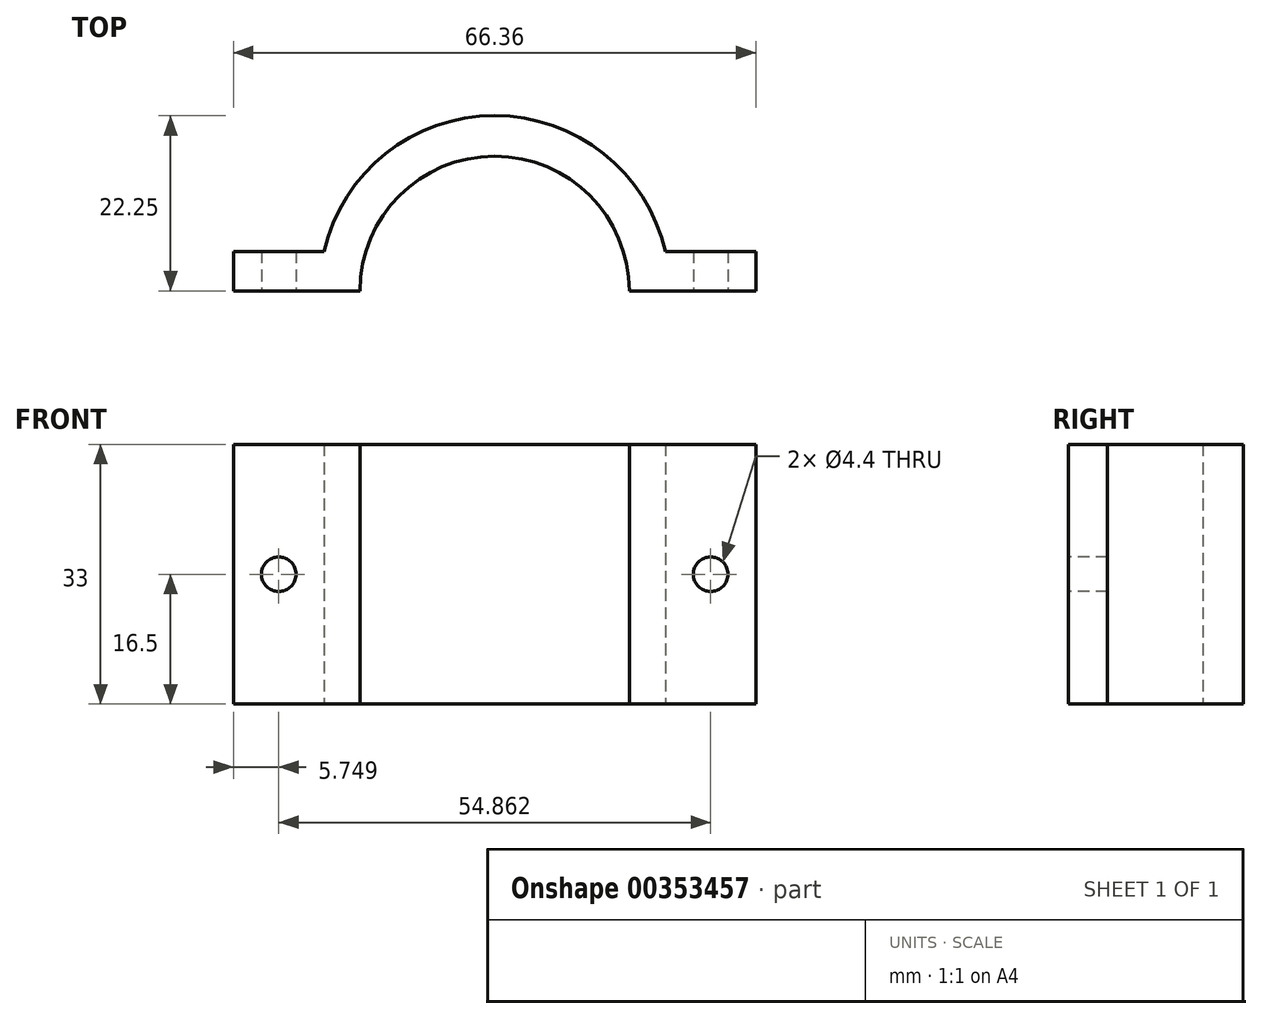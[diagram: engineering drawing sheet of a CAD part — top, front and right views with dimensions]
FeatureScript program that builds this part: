
annotation { "Feature Type Name" : "Feature", "Feature Type Description" : "" }
export const myFeature = defineFeature(function(context is Context, id is Id, definition is map)
    precondition{}
    {
        {
            var Q0;
            Q0=qCreatedBy(makeId("Top.planeOp"),FACE);
            var sketch = newSketch(context, id + "F0", { "sketchPlane" : qUnion([Q0])});
            skCircle(sketch, "E0", {"center": v(0, 0) * mm, "radius": 17.1 * mm});
            skCircle(sketch, "E1", {"center": v(0, 0) * mm, "radius": 22.25 * mm});
            skPoint(sketch, "E2.middle", {"position": v(-27.43, 0) * mm});
            skPoint(sketch, "E3.middle", {"position": v(27.43, 0) * mm});
            skLineSegment(sketch, "E4.bottom", {"start": v(-21.68, -5) * mm, "end": v(-33.18, -5) * mm});
            skLineSegment(sketch, "E4.top", {"start": v(-21.68, 5) * mm, "end": v(-33.18, 5) * mm});
            skLineSegment(sketch, "E4.right", {"start": v(-33.18, -5) * mm, "end": v(-33.18, 5) * mm});
            skLineSegment(sketch, "E5.bottom", {"start": v(21.68, -5) * mm, "end": v(33.18, -5) * mm});
            skLineSegment(sketch, "E5.top", {"start": v(21.68, 5) * mm, "end": v(33.18, 5) * mm});
            skLineSegment(sketch, "E5.right", {"start": v(33.18, -5) * mm, "end": v(33.18, 5) * mm});
            skSolve(sketch);
        }
        {
            var Q0;
            {var subQ0=sQuery(id+"F0.wireOp",EDGE,"E4.bottom");Q0=makeQuery(id+"F0.imprint","IMPRINT",FACE,{"disambiguationData":[TD([[makeQuery(id+"F0.imprint","IMPRINT",EDGE,{"derivedFrom":subQ0}),-1.0]])]});}
            var Q1;
            Q1=makeQuery(id+"F0.imprint","IMPRINT",FACE,{"disambiguationData":[TD([[makeQuery(id+"F0.imprint","IMPRINT",EDGE,{"derivedFrom":sQuery(id+"F0.wireOp",EDGE,"E0")}),-1.0]])]});
            var Q2;
            {var subQ0=sQuery(id+"F0.wireOp",EDGE,"E5.bottom");Q2=makeQuery(id+"F0.imprint","IMPRINT",FACE,{"disambiguationData":[TD([[makeQuery(id+"F0.imprint","IMPRINT",EDGE,{"derivedFrom":subQ0}),1.0]])]});}
            extrude(context, id + "F1", {"entities" : qUnion([Q0, Q1, Q2]), "depth" : 33 * mm});
        }
        {
            var Q0;
            Q0=makeQuery(id+"F1.opExtrude","SWEPT_FACE",FACE,{"disambiguationData":[OSD([sQuery(id+"F0.wireOp",EDGE,"E4.bottom")])]});
            var sketch = newSketch(context, id + "F2", { "sketchPlane" : qUnion([Q0])});
            skLineSegment(sketch, "E6", {"start": v(-27.43, 33) * mm, "end": v(-27.43, 0) * mm, "construction": true});
            skLineSegment(sketch, "E7", {"start": v(-33.18, 16.5) * mm, "end": v(-21.68, 16.5) * mm, "construction": true});
            skPoint(sketch, "E8", {"position": v(-27.43, 16.5) * mm});
            skSolve(sketch);
        }
        {
            var Q0;
            Q0=sQuery(id+"F2.wireOp",VERTEX,"E8");
            var Q1;
            Q1=makeQuery(id+"F1.opExtrude","SWEPT_BODY",BODY,{"disambiguationData":[OSD([sQuery(id+"F0.wireOp",EDGE,"E0"),sQuery(id+"F0.wireOp",EDGE,"E1"),sQuery(id+"F0.wireOp",EDGE,"E4.bottom"),sQuery(id+"F0.wireOp",EDGE,"E4.top"),sQuery(id+"F0.wireOp",EDGE,"E4.right"),sQuery(id+"F0.wireOp",EDGE,"E5.bottom"),sQuery(id+"F0.wireOp",EDGE,"E5.top"),sQuery(id+"F0.wireOp",EDGE,"E5.right")])]});
            hole(context, id + "F3", {"style" : HoleStyle.SIMPLE, "endStyle" : HoleEndStyle.THROUGH, "standardTappedOrClearance" : lookupTablePath({ "standard" : "ISO", "fit" : "Normal", "size" : "M4", "type" : "Clearance" }), "standardBlindInLast" : lookupTablePath({ "fit" : "Standard", "standard" : "ISO", "size" : "M4", "type" : "Clearance" }), "holeDiameter" : 4.4 * mm, "isTappedThrough" : true, "tappedDepth" : 12 * mm, "tapClearance" : 3, "startFromSketch" : true, "locations" : qUnion([Q0]), "scope" : qUnion([Q1])});
        }
        {
            var Q0;
            Q0=makeQuery(id+"F1.opExtrude","SWEPT_FACE",FACE,{"disambiguationData":[OSD([sQuery(id+"F0.wireOp",EDGE,"E5.bottom")])]});
            var sketch = newSketch(context, id + "F4", { "sketchPlane" : qUnion([Q0])});
            skLineSegment(sketch, "E9", {"start": v(27.43, 33) * mm, "end": v(27.43, 0) * mm, "construction": true});
            skLineSegment(sketch, "E10", {"start": v(21.68, 16.5) * mm, "end": v(33.18, 16.5) * mm, "construction": true});
            skPoint(sketch, "E11", {"position": v(27.43, 16.5) * mm});
            skSolve(sketch);
        }
        {
            var Q0;
            Q0=sQuery(id+"F4.wireOp",VERTEX,"E11");
            var Q1;
            Q1=makeQuery(id+"F1.opExtrude","SWEPT_BODY",BODY,{"disambiguationData":[OSD([sQuery(id+"F0.wireOp",EDGE,"E0"),sQuery(id+"F0.wireOp",EDGE,"E1"),sQuery(id+"F0.wireOp",EDGE,"E4.bottom"),sQuery(id+"F0.wireOp",EDGE,"E4.top"),sQuery(id+"F0.wireOp",EDGE,"E4.right"),sQuery(id+"F0.wireOp",EDGE,"E5.bottom"),sQuery(id+"F0.wireOp",EDGE,"E5.top"),sQuery(id+"F0.wireOp",EDGE,"E5.right")])]});
            hole(context, id + "F5", {"style" : HoleStyle.SIMPLE, "endStyle" : HoleEndStyle.THROUGH, "standardTappedOrClearance" : lookupTablePath({ "standard" : "ISO", "fit" : "Normal", "size" : "M4", "type" : "Clearance" }), "standardBlindInLast" : lookupTablePath({ "fit" : "Standard", "standard" : "ISO", "size" : "M4", "type" : "Clearance" }), "holeDiameter" : 4.4 * mm, "isTappedThrough" : true, "tappedDepth" : 12 * mm, "tapClearance" : 3, "startFromSketch" : true, "locations" : qUnion([Q0]), "scope" : qUnion([Q1])});
        }
        {
            var Q0;
            Q0=makeQuery(id+"F1.opExtrude","CAP_FACE",FACE,{"disambiguationData":[OSD([sQuery(id+"F0.wireOp",EDGE,"E0"),sQuery(id+"F0.wireOp",EDGE,"E1"),sQuery(id+"F0.wireOp",EDGE,"E4.bottom"),sQuery(id+"F0.wireOp",EDGE,"E4.top"),sQuery(id+"F0.wireOp",EDGE,"E4.right"),sQuery(id+"F0.wireOp",EDGE,"E5.bottom"),sQuery(id+"F0.wireOp",EDGE,"E5.top"),sQuery(id+"F0.wireOp",EDGE,"E5.right")])],"isStart":false});
            var sketch = newSketch(context, id + "F6", { "sketchPlane" : qUnion([Q0])});
            skLineSegment(sketch, "E12.bottom", {"start": v(-33.18, 0) * mm, "end": v(33.18, 0) * mm});
            skLineSegment(sketch, "E12.top", {"start": v(-33.18, -22.68) * mm, "end": v(33.18, -22.68) * mm});
            skLineSegment(sketch, "E12.left", {"start": v(-33.18, 0) * mm, "end": v(-33.18, -22.68) * mm});
            skLineSegment(sketch, "E12.right", {"start": v(33.18, 0) * mm, "end": v(33.18, -22.68) * mm});
            skSolve(sketch);
        }
        {
            var Q0;
            {var subQ8=sQuery(id+"F0.wireOp",EDGE,"E4.bottom");var subQ9=makeQuery(id+"F1.opExtrude","CAP_EDGE",EDGE,{"disambiguationData":[OSD([subQ8])],"isStart":false});Q0=makeQuery(id+"F6.imprint","IMPRINT",FACE,{"disambiguationData":[TD([[makeQuery(id+"F6.imprint","IMPRINT",EDGE,{"derivedFrom":subQ9}),-1.0]])]});}
            var Q1;
            {var subQ3=sQuery(id+"F6.wireOp",EDGE,"E12.top");Q1=makeQuery(id+"F6.imprint","IMPRINT",FACE,{"disambiguationData":[TD([[makeQuery(id+"F6.imprint","IMPRINT",EDGE,{"derivedFrom":subQ3}),1.0]])]});}
            var Q2;
            {var subQ0=sQuery(id+"F6.wireOp",EDGE,"E12.bottom");var subQ1=makeQuery(id+"F1.opExtrude","CAP_EDGE",EDGE,{"disambiguationData":[OSD([sQuery(id+"F0.wireOp",EDGE,"E0")])],"isStart":false});var subQ2=makeQuery(id+"F6.imprint","INTERSECT",VERTEX,{"disambiguationData":[OD(0.0)],"derivedFrom":[subQ1,subQ0]});Q2=makeQuery(id+"F6.imprint","IMPRINT",FACE,{"disambiguationData":[TD([[makeQuery(id+"F6.imprint","IMPRINT",EDGE,{"disambiguationData":[TD([[subQ2,-1.0]])],"derivedFrom":subQ0}),-1.0]])]});}
            extrude(context, id + "F7", {"entities" : qUnion([Q0, Q1, Q2]), "operationType" : NewBodyOperationType.REMOVE, "oppositeDirection" : true, "depth" : 33 * mm});
        }
    });
